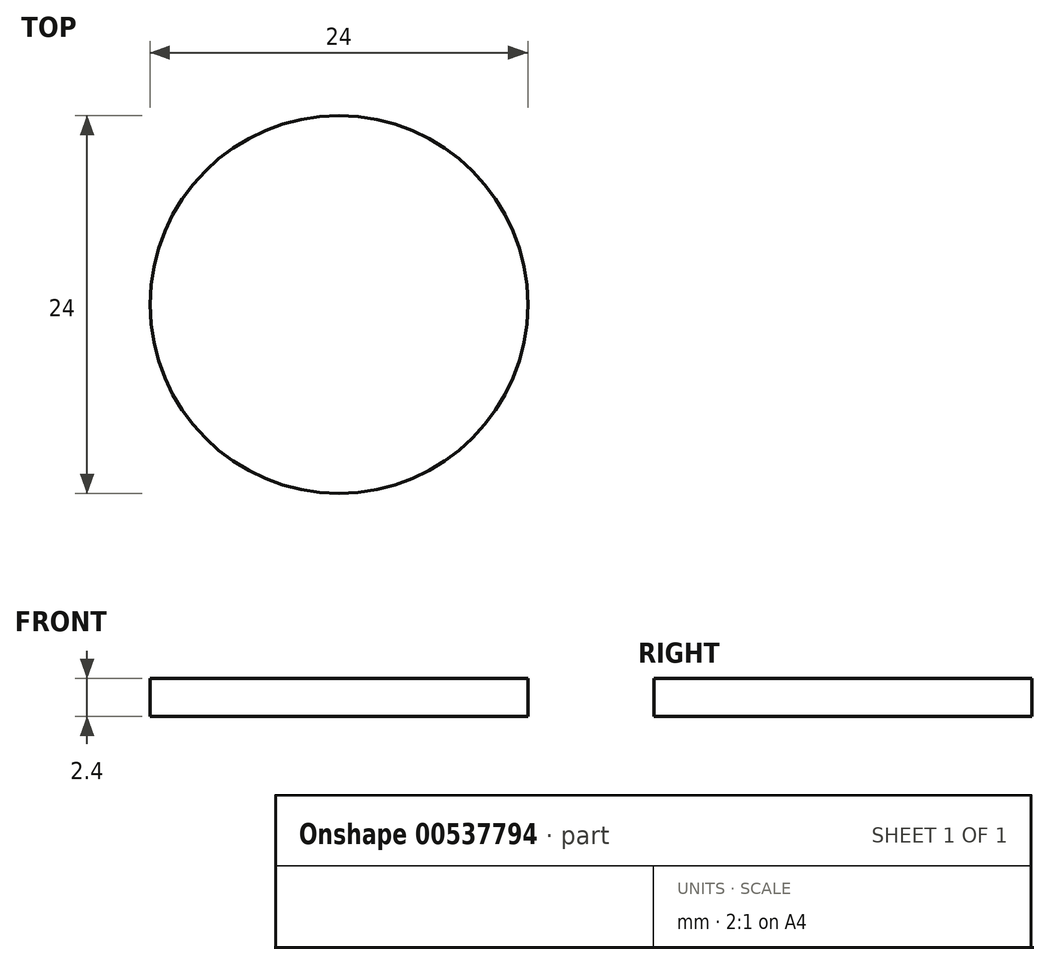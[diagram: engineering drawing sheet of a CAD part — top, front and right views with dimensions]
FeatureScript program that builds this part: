
annotation { "Feature Type Name" : "Feature", "Feature Type Description" : "" }
export const myFeature = defineFeature(function(context is Context, id is Id, definition is map)
    precondition{}
    {
        {
            var Q0;
            Q0=qCreatedBy(makeId("Top.planeOp"),FACE);
            var sketch = newSketch(context, id + "F0", { "sketchPlane" : qUnion([Q0])});
            skCircle(sketch, "E0", {"center": v(-18.1, 22.95) * mm, "radius": 12 * mm});
            skSolve(sketch);
        }
        {
            var Q0;
            Q0 = qSketchRegion(id + "F0", true);
            extrude(context, id + "F1", {"entities" : qUnion([Q0]), "depth" : 2.4 * mm, "offsetDistance" : 25 * mm});
        }
    });
